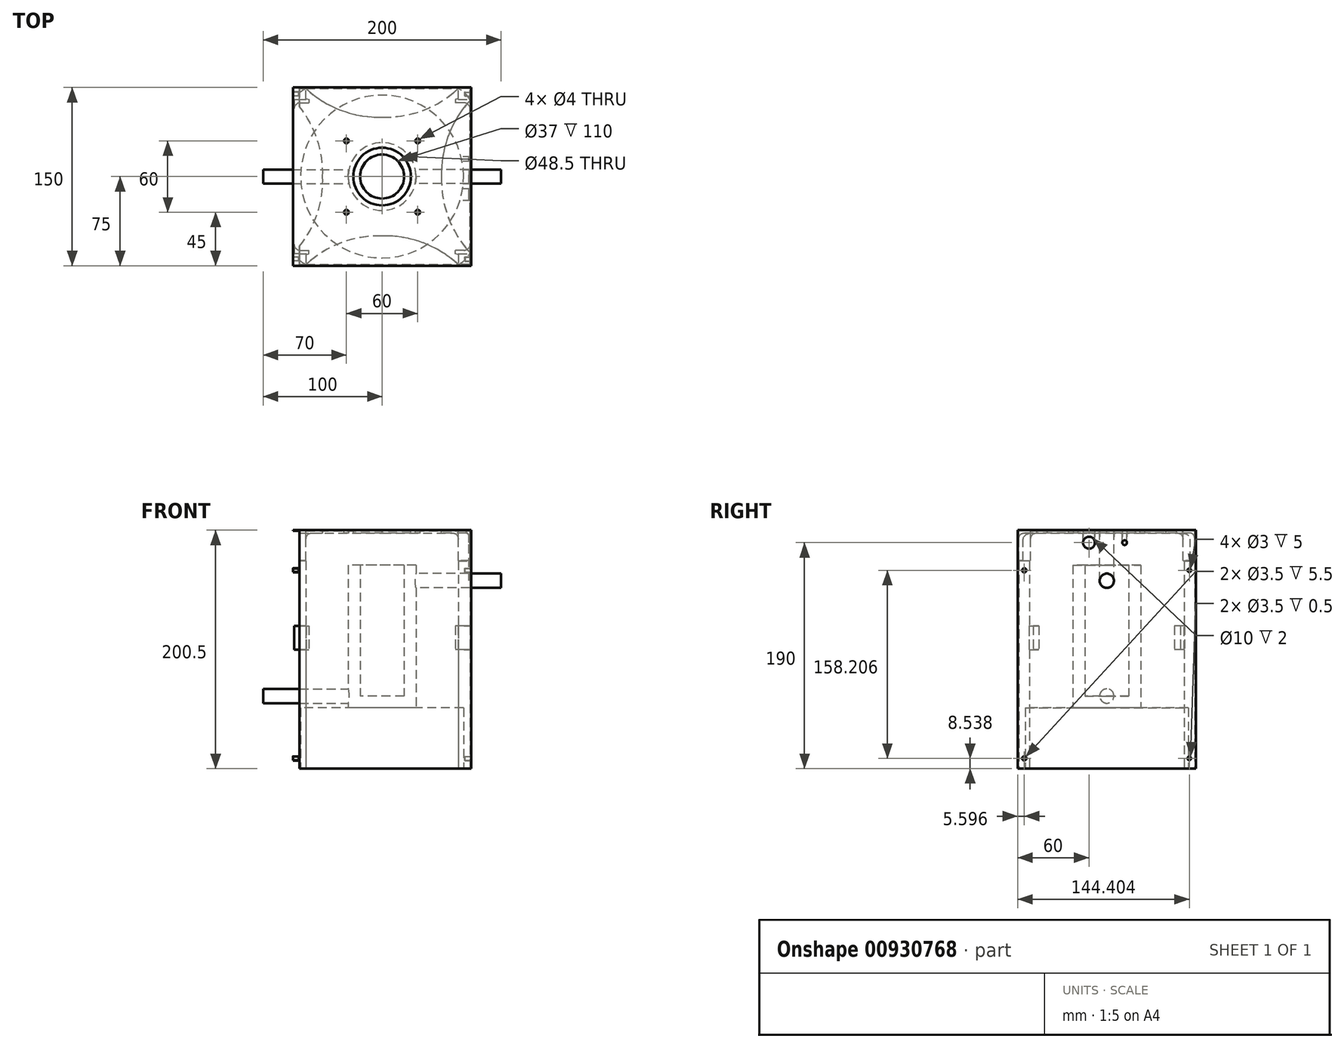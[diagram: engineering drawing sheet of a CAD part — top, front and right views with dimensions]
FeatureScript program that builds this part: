
annotation { "Feature Type Name" : "Feature", "Feature Type Description" : "" }
export const myFeature = defineFeature(function(context is Context, id is Id, definition is map)
    precondition{}
    {
        {
            var Q0;
            Q0=qCreatedBy(makeId("Top.planeOp"),FACE);
            var sketch = newSketch(context, id + "F0", { "sketchPlane" : qUnion([Q0])});
            skCircle(sketch, "E0", {"center": v(0, 0) * mm, "radius": 68.5 * mm});
            skSolve(sketch);
        }
        {
            var Q0;
            Q0 = qSketchRegion(id + "F0", true);
            extrude(context, id + "F1", {"entities" : qUnion([Q0]), "depth" : 51 * mm, "offsetDistance" : 25 * mm});
        }
        {
            var Q0;
            Q0=makeQuery(id+"F1.opExtrude","CAP_FACE",FACE,{"disambiguationData":[OSD([sQuery(id+"F0.wireOp",EDGE,"E0")])],"isStart":false});
            var sketch = newSketch(context, id + "F2", { "sketchPlane" : qUnion([Q0])});
            skCircle(sketch, "E1", {"center": v(0, 0) * mm, "radius": 28.5 * mm});
            skSolve(sketch);
        }
        {
            var Q0;
            Q0 = qSketchRegion(id + "F2", true);
            extrude(context, id + "F3", {"entities" : qUnion([Q0]), "depth" : 120 * mm, "offsetDistance" : 25 * mm});
        }
        {
            var Q0;
            Q0=qCreatedBy(makeId("Right.planeOp"),FACE);
            var sketch = newSketch(context, id + "F4", { "sketchPlane" : qUnion([Q0])});
            skCircle(sketch, "E2", {"center": v(0, 158) * mm, "radius": 6 * mm});
            skCircle(sketch, "E3", {"center": v(0, 61) * mm, "radius": 6 * mm});
            skSolve(sketch);
        }
        {
            var Q0;
            Q0=makeQuery(id+"F4.imprint","IMPRINT",FACE,{"disambiguationData":[TD([[makeQuery(id+"F4.imprint","IMPRINT",EDGE,{"derivedFrom":sQuery(id+"F4.wireOp",EDGE,"E2")}),1.0]])]});
            extrude(context, id + "F5", {"entities" : qUnion([Q0]), "operationType" : NewBodyOperationType.ADD, "depth" : 100 * mm, "offsetDistance" : 25 * mm});
        }
        {
            var Q0;
            Q0=makeQuery(id+"F4.imprint","IMPRINT",FACE,{"disambiguationData":[TD([[makeQuery(id+"F4.imprint","IMPRINT",EDGE,{"derivedFrom":sQuery(id+"F4.wireOp",EDGE,"E3")}),1.0]])]});
            extrude(context, id + "F6", {"entities" : qUnion([Q0]), "operationType" : NewBodyOperationType.ADD, "oppositeDirection" : true, "depth" : 100 * mm, "offsetDistance" : 25 * mm});
        }
        {
            var Q0;
            Q0=makeQuery(id+"F3.opExtrude","CAP_FACE",FACE,{"disambiguationData":[OSD([sQuery(id+"F2.wireOp",EDGE,"E1")])],"isStart":false});
            shell(context, id + "F7", {"entities" : qUnion([Q0]), "thickness" : 10 * mm});
        }
        {
            var Q0;
            Q0=qCreatedBy(makeId("Front.planeOp"),FACE);
            var sketch = newSketch(context, id + "F8", { "sketchPlane" : qUnion([Q0])});
            skLineSegment(sketch, "E4.bottom", {"start": v(-75, 0) * mm, "end": v(75, 0) * mm});
            skLineSegment(sketch, "E4.top", {"start": v(-75, 180) * mm, "end": v(75, 180) * mm});
            skLineSegment(sketch, "E4.left", {"start": v(-75, 0) * mm, "end": v(-75, 180) * mm});
            skLineSegment(sketch, "E4.right", {"start": v(75, 0) * mm, "end": v(75, 180) * mm});
            skSolve(sketch);
        }
        {
            var Q0;
            Q0=qCreatedBy(makeId("Top.planeOp"),FACE);
            cPlane(context, id + "F9", {"entities" : qUnion([Q0]), "cplaneType" : CPlaneType.OFFSET, "offset" : 200 * mm, "width" : 150 * mm, "height" : 150 * mm});
        }
        {
            var Q0;
            Q0=qCreatedBy(id+"F9.planeOp",FACE);
            var sketch = newSketch(context, id + "F10", { "sketchPlane" : qUnion([Q0])});
            skCircle(sketch, "E5", {"center": v(0, 0) * mm, "radius": 24.25 * mm});
            skCircle(sketch, "E6", {"center": v(-30, 30) * mm, "radius": 2 * mm});
            skCircle(sketch, "E7.1.0", {"center": v(-30, -30) * mm, "radius": 2 * mm});
            skCircle(sketch, "E7.2.0", {"center": v(30, -30) * mm, "radius": 2 * mm});
            skCircle(sketch, "E7.3.0", {"center": v(30, 30) * mm, "radius": 2 * mm});
            skLineSegment(sketch, "E8.bottom", {"start": v(75, 75) * mm, "end": v(-75, 75) * mm});
            skLineSegment(sketch, "E8.top", {"start": v(75, -75) * mm, "end": v(-75, -75) * mm});
            skLineSegment(sketch, "E8.left", {"start": v(75, 75) * mm, "end": v(75, -75) * mm});
            skLineSegment(sketch, "E8.right", {"start": v(-75, 75) * mm, "end": v(-75, -75) * mm});
            skLineSegment(sketch, "E9.bottom", {"start": v(-74, 74) * mm, "end": v(-64, 74) * mm});
            skLineSegment(sketch, "E9.top", {"start": v(-74, 64) * mm, "end": v(-64, 64) * mm});
            skLineSegment(sketch, "E9.left", {"start": v(-74, 74) * mm, "end": v(-74, 64) * mm});
            skLineSegment(sketch, "E9.right", {"start": v(-64, 74) * mm, "end": v(-64, 64) * mm});
            skArc(sketch, "E10", {"start": v(-64, 74) * mm, "mid": v(-69.91, 69.91) * mm, "end": v(-74, 64) * mm});
            skLineSegment(sketch, "E11.1.0", {"start": v(-74, -74) * mm, "end": v(-74, -64) * mm});
            skLineSegment(sketch, "E11.1.1", {"start": v(-74, -74) * mm, "end": v(-64, -74) * mm});
            skArc(sketch, "E11.1.2", {"start": v(-74, -64) * mm, "mid": v(-69.91, -69.91) * mm, "end": v(-64, -74) * mm});
            skLineSegment(sketch, "E11.2.0", {"start": v(74, -74) * mm, "end": v(64, -74) * mm});
            skLineSegment(sketch, "E11.2.1", {"start": v(74, -74) * mm, "end": v(74, -64) * mm});
            skArc(sketch, "E11.2.2", {"start": v(64, -74) * mm, "mid": v(69.91, -69.91) * mm, "end": v(74, -64) * mm});
            skLineSegment(sketch, "E11.3.0", {"start": v(74, 74) * mm, "end": v(74, 64) * mm});
            skLineSegment(sketch, "E11.3.1", {"start": v(74, 74) * mm, "end": v(64, 74) * mm});
            skArc(sketch, "E11.3.2", {"start": v(74, 64) * mm, "mid": v(69.91, 69.91) * mm, "end": v(64, 74) * mm});
            skCircle(sketch, "E12", {"center": v(0, 0) * mm, "radius": 50 * mm});
            skArc(sketch, "E13", {"start": v(-50, 0) * mm, "mid": v(-55.69, 34.37) * mm, "end": v(-74, 64) * mm});
            skArc(sketch, "E14", {"start": v(-64, 74) * mm, "mid": v(-34.37, 55.69) * mm, "end": v(0, 50) * mm});
            skArc(sketch, "E15.1.0", {"start": v(-74, -64) * mm, "mid": v(-55.69, -34.37) * mm, "end": v(-50, 0) * mm});
            skArc(sketch, "E15.1.1", {"start": v(0, -50) * mm, "mid": v(-34.37, -55.69) * mm, "end": v(-64, -74) * mm});
            skArc(sketch, "E15.2.0", {"start": v(64, -74) * mm, "mid": v(34.37, -55.69) * mm, "end": v(0, -50) * mm});
            skArc(sketch, "E15.2.1", {"start": v(50, 0) * mm, "mid": v(55.69, -34.37) * mm, "end": v(74, -64) * mm});
            skArc(sketch, "E15.3.0", {"start": v(74, 64) * mm, "mid": v(55.69, 34.37) * mm, "end": v(50, 0) * mm});
            skArc(sketch, "E15.3.1", {"start": v(0, 50) * mm, "mid": v(34.37, 55.69) * mm, "end": v(64, 74) * mm});
            skSolve(sketch);
        }
        {
            var Q0;
            Q0=qCreatedBy(id+"F9.planeOp",FACE);
            var sketch = newSketch(context, id + "F11", { "sketchPlane" : qUnion([Q0])});
            skLineSegment(sketch, "E16.bottom", {"start": v(75, 75) * mm, "end": v(-75, 75) * mm});
            skLineSegment(sketch, "E16.top", {"start": v(75, -75) * mm, "end": v(-75, -75) * mm});
            skLineSegment(sketch, "E16.left", {"start": v(75, 75) * mm, "end": v(75, -75) * mm});
            skLineSegment(sketch, "E16.right", {"start": v(-75, 75) * mm, "end": v(-75, -75) * mm});
            skPoint(sketch, "E16.middle", {"position": v(0, 0) * mm});
            skSolve(sketch);
        }
        {
            var Q0;
            Q0=makeQuery(id+"F10.imprint","IMPRINT",FACE,{"disambiguationData":[TD([[makeQuery(id+"F10.imprint","IMPRINT",EDGE,{"derivedFrom":sQuery(id+"F10.wireOp",EDGE,"E9.bottom")}),-1.0]])]});
            var Q1;
            Q1=makeQuery(id+"F10.imprint","IMPRINT",FACE,{"disambiguationData":[TD([[makeQuery(id+"F10.imprint","IMPRINT",EDGE,{"derivedFrom":sQuery(id+"F10.wireOp",EDGE,"E9.top")}),1.0]])]});
            var Q2;
            {var subQ2=sQuery(id+"F10.wireOp",EDGE,"E9.top");Q2=makeQuery(id+"F10.imprint","IMPRINT",FACE,{"disambiguationData":[TD([[makeQuery(id+"F10.imprint","IMPRINT",EDGE,{"derivedFrom":subQ2}),-1.0]])]});}
            var Q3;
            Q3=makeQuery(id+"F10.imprint","IMPRINT",FACE,{"disambiguationData":[TD([[makeQuery(id+"F10.imprint","IMPRINT",EDGE,{"derivedFrom":sQuery(id+"F10.wireOp",EDGE,"E5")}),-1.0]])]});
            var Q4;
            {var subQ0=sQuery(id+"F10.wireOp",EDGE,"E11.3.2");Q4=makeQuery(id+"F10.imprint","IMPRINT",FACE,{"disambiguationData":[TD([[makeQuery(id+"F10.imprint","IMPRINT",EDGE,{"derivedFrom":subQ0}),1.0]])]});}
            var Q5;
            Q5=makeQuery(id+"F10.imprint","IMPRINT",FACE,{"disambiguationData":[TD([[makeQuery(id+"F10.imprint","IMPRINT",EDGE,{"derivedFrom":sQuery(id+"F10.wireOp",EDGE,"E11.3.0")}),-1.0]])]});
            var Q6;
            Q6=makeQuery(id+"F10.imprint","IMPRINT",FACE,{"disambiguationData":[TD([[makeQuery(id+"F10.imprint","IMPRINT",EDGE,{"derivedFrom":sQuery(id+"F10.wireOp",EDGE,"E11.2.0")}),-1.0]])]});
            var Q7;
            {var subQ0=sQuery(id+"F10.wireOp",EDGE,"E11.2.2");Q7=makeQuery(id+"F10.imprint","IMPRINT",FACE,{"disambiguationData":[TD([[makeQuery(id+"F10.imprint","IMPRINT",EDGE,{"derivedFrom":subQ0}),1.0]])]});}
            var Q8;
            {var subQ0=sQuery(id+"F10.wireOp",EDGE,"E11.1.2");Q8=makeQuery(id+"F10.imprint","IMPRINT",FACE,{"disambiguationData":[TD([[makeQuery(id+"F10.imprint","IMPRINT",EDGE,{"derivedFrom":subQ0}),1.0]])]});}
            var Q9;
            Q9=makeQuery(id+"F10.imprint","IMPRINT",FACE,{"disambiguationData":[TD([[makeQuery(id+"F10.imprint","IMPRINT",EDGE,{"derivedFrom":sQuery(id+"F10.wireOp",EDGE,"E11.1.0")}),-1.0]])]});
            extrude(context, id + "F12", {"entities" : qUnion([Q0, Q1, Q2, Q3, Q4, Q5, Q6, Q7, Q8, Q9]), "oppositeDirection" : true, "depth" : 2 * mm, "offsetDistance" : 25 * mm});
        }
        {
            var Q0;
            Q0 = qSketchRegion(id + "F11", true);
            extrude(context, id + "F13", {"entities" : qUnion([Q0]), "operationType" : NewBodyOperationType.ADD, "depth" : 0.5 * mm, "offsetDistance" : 25 * mm});
        }
        {
            var Q0;
            Q0=makeQuery(id+"F10.imprint","IMPRINT",FACE,{"disambiguationData":[TD([[makeQuery(id+"F10.imprint","IMPRINT",EDGE,{"derivedFrom":sQuery(id+"F10.wireOp",EDGE,"E9.bottom")}),-1.0]])]});
            var Q1;
            Q1=makeQuery(id+"F10.imprint","IMPRINT",FACE,{"disambiguationData":[TD([[makeQuery(id+"F10.imprint","IMPRINT",EDGE,{"derivedFrom":sQuery(id+"F10.wireOp",EDGE,"E11.1.0")}),-1.0]])]});
            var Q2;
            Q2=makeQuery(id+"F10.imprint","IMPRINT",FACE,{"disambiguationData":[TD([[makeQuery(id+"F10.imprint","IMPRINT",EDGE,{"derivedFrom":sQuery(id+"F10.wireOp",EDGE,"E11.2.0")}),-1.0]])]});
            var Q3;
            Q3=makeQuery(id+"F10.imprint","IMPRINT",FACE,{"disambiguationData":[TD([[makeQuery(id+"F10.imprint","IMPRINT",EDGE,{"derivedFrom":sQuery(id+"F10.wireOp",EDGE,"E11.3.0")}),-1.0]])]});
            extrude(context, id + "F14", {"entities" : qUnion([Q0, Q1, Q2, Q3]), "operationType" : NewBodyOperationType.ADD, "oppositeDirection" : true, "depth" : 25 * mm, "offsetDistance" : 25 * mm});
        }
        {
            var Q0;
            Q0=makeQuery(id+"F10.imprint","IMPRINT",FACE,{"disambiguationData":[TD([[makeQuery(id+"F10.imprint","IMPRINT",EDGE,{"derivedFrom":sQuery(id+"F10.wireOp",EDGE,"E6")}),1.0]])]});
            var Q1;
            Q1=makeQuery(id+"F10.imprint","IMPRINT",FACE,{"disambiguationData":[TD([[makeQuery(id+"F10.imprint","IMPRINT",EDGE,{"derivedFrom":sQuery(id+"F10.wireOp",EDGE,"E7.3.0")}),1.0]])]});
            var Q2;
            Q2=makeQuery(id+"F10.imprint","IMPRINT",FACE,{"disambiguationData":[TD([[makeQuery(id+"F10.imprint","IMPRINT",EDGE,{"derivedFrom":sQuery(id+"F10.wireOp",EDGE,"E7.2.0")}),1.0]])]});
            var Q3;
            Q3=makeQuery(id+"F10.imprint","IMPRINT",FACE,{"disambiguationData":[TD([[makeQuery(id+"F10.imprint","IMPRINT",EDGE,{"derivedFrom":sQuery(id+"F10.wireOp",EDGE,"E7.1.0")}),1.0]])]});
            var Q4;
            Q4=makeQuery(id+"F10.imprint","IMPRINT",FACE,{"disambiguationData":[TD([[makeQuery(id+"F10.imprint","IMPRINT",EDGE,{"derivedFrom":sQuery(id+"F10.wireOp",EDGE,"E5")}),1.0]])]});
            extrude(context, id + "F15", {"entities" : qUnion([Q0, Q1, Q2, Q3, Q4]), "operationType" : NewBodyOperationType.REMOVE, "endBound" : BoundingType.SYMMETRIC, "oppositeDirection" : true, "depth" : 25 * mm, "offsetDistance" : 25 * mm});
        }
        {
            var Q0;
            Q0=makeQuery(id+"F14.boolean.opBoolean","INTERSECT",EDGE,{"derivedFrom":[makeQuery(id+"F12.opExtrude","CAP_FACE",FACE,{"disambiguationData":[OSD([sQuery(id+"F10.wireOp",EDGE,"E5"),sQuery(id+"F10.wireOp",EDGE,"E6"),sQuery(id+"F10.wireOp",EDGE,"E7.1.0"),sQuery(id+"F10.wireOp",EDGE,"E7.2.0"),sQuery(id+"F10.wireOp",EDGE,"E7.3.0"),sQuery(id+"F10.wireOp",EDGE,"E9.bottom"),sQuery(id+"F10.wireOp",EDGE,"E9.left"),sQuery(id+"F10.wireOp",EDGE,"E11.1.0"),sQuery(id+"F10.wireOp",EDGE,"E11.1.1"),sQuery(id+"F10.wireOp",EDGE,"E11.2.0"),sQuery(id+"F10.wireOp",EDGE,"E11.2.1"),sQuery(id+"F10.wireOp",EDGE,"E11.3.0"),sQuery(id+"F10.wireOp",EDGE,"E11.3.1"),sQuery(id+"F10.wireOp",EDGE,"E13"),sQuery(id+"F10.wireOp",EDGE,"E14"),sQuery(id+"F10.wireOp",EDGE,"E15.1.0"),sQuery(id+"F10.wireOp",EDGE,"E15.1.1"),sQuery(id+"F10.wireOp",EDGE,"E15.2.0"),sQuery(id+"F10.wireOp",EDGE,"E15.2.1"),sQuery(id+"F10.wireOp",EDGE,"E15.3.0"),sQuery(id+"F10.wireOp",EDGE,"E15.3.1")])],"isStart":false}),makeQuery(id+"F14.opExtrude","SWEPT_FACE",FACE,{"disambiguationData":[OSD([sQuery(id+"F10.wireOp",EDGE,"E11.1.2")])]})]});
            var Q1;
            Q1=makeQuery(id+"F14.boolean.opBoolean","INTERSECT",EDGE,{"derivedFrom":[makeQuery(id+"F12.opExtrude","CAP_FACE",FACE,{"disambiguationData":[OSD([sQuery(id+"F10.wireOp",EDGE,"E5"),sQuery(id+"F10.wireOp",EDGE,"E6"),sQuery(id+"F10.wireOp",EDGE,"E7.1.0"),sQuery(id+"F10.wireOp",EDGE,"E7.2.0"),sQuery(id+"F10.wireOp",EDGE,"E7.3.0"),sQuery(id+"F10.wireOp",EDGE,"E9.bottom"),sQuery(id+"F10.wireOp",EDGE,"E9.left"),sQuery(id+"F10.wireOp",EDGE,"E11.1.0"),sQuery(id+"F10.wireOp",EDGE,"E11.1.1"),sQuery(id+"F10.wireOp",EDGE,"E11.2.0"),sQuery(id+"F10.wireOp",EDGE,"E11.2.1"),sQuery(id+"F10.wireOp",EDGE,"E11.3.0"),sQuery(id+"F10.wireOp",EDGE,"E11.3.1"),sQuery(id+"F10.wireOp",EDGE,"E13"),sQuery(id+"F10.wireOp",EDGE,"E14"),sQuery(id+"F10.wireOp",EDGE,"E15.1.0"),sQuery(id+"F10.wireOp",EDGE,"E15.1.1"),sQuery(id+"F10.wireOp",EDGE,"E15.2.0"),sQuery(id+"F10.wireOp",EDGE,"E15.2.1"),sQuery(id+"F10.wireOp",EDGE,"E15.3.0"),sQuery(id+"F10.wireOp",EDGE,"E15.3.1")])],"isStart":false}),makeQuery(id+"F14.opExtrude","SWEPT_FACE",FACE,{"disambiguationData":[OSD([sQuery(id+"F10.wireOp",EDGE,"E11.3.2")])]})]});
            var Q2;
            Q2=makeQuery(id+"F14.boolean.opBoolean","INTERSECT",EDGE,{"derivedFrom":[makeQuery(id+"F12.opExtrude","CAP_FACE",FACE,{"disambiguationData":[OSD([sQuery(id+"F10.wireOp",EDGE,"E5"),sQuery(id+"F10.wireOp",EDGE,"E6"),sQuery(id+"F10.wireOp",EDGE,"E7.1.0"),sQuery(id+"F10.wireOp",EDGE,"E7.2.0"),sQuery(id+"F10.wireOp",EDGE,"E7.3.0"),sQuery(id+"F10.wireOp",EDGE,"E9.bottom"),sQuery(id+"F10.wireOp",EDGE,"E9.left"),sQuery(id+"F10.wireOp",EDGE,"E11.1.0"),sQuery(id+"F10.wireOp",EDGE,"E11.1.1"),sQuery(id+"F10.wireOp",EDGE,"E11.2.0"),sQuery(id+"F10.wireOp",EDGE,"E11.2.1"),sQuery(id+"F10.wireOp",EDGE,"E11.3.0"),sQuery(id+"F10.wireOp",EDGE,"E11.3.1"),sQuery(id+"F10.wireOp",EDGE,"E13"),sQuery(id+"F10.wireOp",EDGE,"E14"),sQuery(id+"F10.wireOp",EDGE,"E15.1.0"),sQuery(id+"F10.wireOp",EDGE,"E15.1.1"),sQuery(id+"F10.wireOp",EDGE,"E15.2.0"),sQuery(id+"F10.wireOp",EDGE,"E15.2.1"),sQuery(id+"F10.wireOp",EDGE,"E15.3.0"),sQuery(id+"F10.wireOp",EDGE,"E15.3.1")])],"isStart":false}),makeQuery(id+"F14.opExtrude","SWEPT_FACE",FACE,{"disambiguationData":[OSD([sQuery(id+"F10.wireOp",EDGE,"E10")])]})]});
            var Q3;
            Q3=makeQuery(id+"F14.boolean.opBoolean","INTERSECT",EDGE,{"derivedFrom":[makeQuery(id+"F12.opExtrude","CAP_FACE",FACE,{"disambiguationData":[OSD([sQuery(id+"F10.wireOp",EDGE,"E5"),sQuery(id+"F10.wireOp",EDGE,"E6"),sQuery(id+"F10.wireOp",EDGE,"E7.1.0"),sQuery(id+"F10.wireOp",EDGE,"E7.2.0"),sQuery(id+"F10.wireOp",EDGE,"E7.3.0"),sQuery(id+"F10.wireOp",EDGE,"E9.bottom"),sQuery(id+"F10.wireOp",EDGE,"E9.left"),sQuery(id+"F10.wireOp",EDGE,"E11.1.0"),sQuery(id+"F10.wireOp",EDGE,"E11.1.1"),sQuery(id+"F10.wireOp",EDGE,"E11.2.0"),sQuery(id+"F10.wireOp",EDGE,"E11.2.1"),sQuery(id+"F10.wireOp",EDGE,"E11.3.0"),sQuery(id+"F10.wireOp",EDGE,"E11.3.1"),sQuery(id+"F10.wireOp",EDGE,"E13"),sQuery(id+"F10.wireOp",EDGE,"E14"),sQuery(id+"F10.wireOp",EDGE,"E15.1.0"),sQuery(id+"F10.wireOp",EDGE,"E15.1.1"),sQuery(id+"F10.wireOp",EDGE,"E15.2.0"),sQuery(id+"F10.wireOp",EDGE,"E15.2.1"),sQuery(id+"F10.wireOp",EDGE,"E15.3.0"),sQuery(id+"F10.wireOp",EDGE,"E15.3.1")])],"isStart":false}),makeQuery(id+"F14.opExtrude","SWEPT_FACE",FACE,{"disambiguationData":[OSD([sQuery(id+"F10.wireOp",EDGE,"E11.2.2")])]})]});
            fillet(context, id + "F16", {"entities" : qUnion([Q0, Q1, Q2, Q3]), "tangentPropagation" : true, "radius" : 5 * mm, "defaultsChanged" : false, "vertexSettings" : [], "allowEdgeOverflow" : false});
        }
        {
            var Q0;
            Q0=makeQuery(id+"F8.imprint","IMPRINT",FACE,{"disambiguationData":[TD([[makeQuery(id+"F8.imprint","IMPRINT",EDGE,{"derivedFrom":sQuery(id+"F8.wireOp",EDGE,"E4.bottom")}),1.0]])]});
            cPlane(context, id + "F17", {"entities" : qUnion([Q0]), "cplaneType" : CPlaneType.OFFSET, "offset" : 75 * mm, "width" : 150 * mm, "height" : 150 * mm});
        }
        {
            var Q0;
            Q0=qCreatedBy(id+"F17.planeOp",FACE);
            var sketch = newSketch(context, id + "F18", { "sketchPlane" : qUnion([Q0])});
            skLineSegment(sketch, "E17.bottom", {"start": v(-75, 0) * mm, "end": v(75, 0) * mm});
            skLineSegment(sketch, "E17.top", {"start": v(-75, 200) * mm, "end": v(75, 200) * mm});
            skLineSegment(sketch, "E17.left", {"start": v(-75, 0) * mm, "end": v(-75, 200) * mm});
            skLineSegment(sketch, "E17.right", {"start": v(75, 0) * mm, "end": v(75, 200) * mm});
            skLineSegment(sketch, "E18", {"start": v(-74, 200) * mm, "end": v(-74, 0) * mm});
            skLineSegment(sketch, "E19", {"start": v(-64, 200) * mm, "end": v(-64, 0) * mm});
            skLineSegment(sketch, "E20", {"start": v(74, 200) * mm, "end": v(74, 0) * mm});
            skLineSegment(sketch, "E21", {"start": v(64, 200) * mm, "end": v(64, 0) * mm});
            skLineSegment(sketch, "E22", {"start": v(-64, 174.5) * mm, "end": v(-74, 174.5) * mm});
            skLineSegment(sketch, "E23", {"start": v(64, 174.5) * mm, "end": v(74, 174.5) * mm});
            skSolve(sketch);
        }
        {
            var Q0;
            {var subQ0=sQuery(id+"F18.wireOp",EDGE,"E19");Q0=makeQuery(id+"F18.imprint","IMPRINT",FACE,{"disambiguationData":[TD([[makeQuery(id+"F18.imprint","IMPRINT",EDGE,{"derivedFrom":subQ0}),1.0]])]});}
            var Q1;
            {var subQ0=sQuery(id+"F18.wireOp",EDGE,"E20");Q1=makeQuery(id+"F18.imprint","IMPRINT",FACE,{"disambiguationData":[TD([[makeQuery(id+"F18.imprint","IMPRINT",EDGE,{"derivedFrom":subQ0}),-1.0]])]});}
            var Q2;
            {var subQ5=sQuery(id+"F18.wireOp",EDGE,"E22");Q2=makeQuery(id+"F18.imprint","IMPRINT",FACE,{"disambiguationData":[TD([[makeQuery(id+"F18.imprint","IMPRINT",EDGE,{"derivedFrom":subQ5}),-1.0]])]});}
            var Q3;
            {var subQ5=sQuery(id+"F18.wireOp",EDGE,"E22");Q3=makeQuery(id+"F18.imprint","IMPRINT",FACE,{"disambiguationData":[TD([[makeQuery(id+"F18.imprint","IMPRINT",EDGE,{"derivedFrom":subQ5}),1.0]])]});}
            extrude(context, id + "F19", {"entities" : qUnion([Q0, Q1, Q2, Q3]), "oppositeDirection" : true, "depth" : 1 * mm, "offsetDistance" : 25 * mm});
        }
        {
            var Q0;
            {var subQ5=sQuery(id+"F18.wireOp",EDGE,"E22");Q0=makeQuery(id+"F18.imprint","IMPRINT",FACE,{"disambiguationData":[TD([[makeQuery(id+"F18.imprint","IMPRINT",EDGE,{"derivedFrom":subQ5}),1.0]])]});}
            var Q1;
            {var subQ5=sQuery(id+"F18.wireOp",EDGE,"E23");Q1=makeQuery(id+"F18.imprint","IMPRINT",FACE,{"disambiguationData":[TD([[makeQuery(id+"F18.imprint","IMPRINT",EDGE,{"derivedFrom":subQ5}),-1.0]])]});}
            extrude(context, id + "F20", {"entities" : qUnion([Q0, Q1]), "operationType" : NewBodyOperationType.ADD, "oppositeDirection" : true, "depth" : 10 * mm, "offsetDistance" : 25 * mm});
        }
        {
            var Q0;
            Q0=qCreatedBy(makeId("Right.planeOp"),FACE);
            cPlane(context, id + "F21", {"entities" : qUnion([Q0]), "cplaneType" : CPlaneType.OFFSET, "offset" : 75 * mm, "width" : 150 * mm, "height" : 150 * mm});
        }
        {
            var Q0;
            Q0=qCreatedBy(id+"F21.planeOp",FACE);
            var sketch = newSketch(context, id + "F22", { "sketchPlane" : qUnion([Q0])});
            skLineSegment(sketch, "E24.bottom", {"start": v(-75, 0) * mm, "end": v(75, 0) * mm});
            skLineSegment(sketch, "E24.top", {"start": v(-75, 200) * mm, "end": v(75, 200) * mm});
            skLineSegment(sketch, "E24.left", {"start": v(-75, 0) * mm, "end": v(-75, 200) * mm});
            skLineSegment(sketch, "E24.right", {"start": v(75, 0) * mm, "end": v(75, 200) * mm});
            skCircle(sketch, "E25.0", {"center": v(0, 158) * mm, "radius": 6 * mm});
            skCircle(sketch, "E26", {"center": v(-15, 190) * mm, "radius": 5 * mm});
            skCircle(sketch, "E27", {"center": v(15, 190) * mm, "radius": 2 * mm});
            skLineSegment(sketch, "E28", {"start": v(15, 190) * mm, "end": v(-15, 190) * mm, "construction": true});
            skLineSegment(sketch, "E29", {"start": v(0, 0) * mm, "end": v(0, 190) * mm, "construction": true});
            skLineSegment(sketch, "E30", {"start": v(6, 158) * mm, "end": v(6, 200) * mm});
            skLineSegment(sketch, "E31", {"start": v(-6, 158) * mm, "end": v(-6, 200) * mm});
            skLineSegment(sketch, "E32", {"start": v(-10, 190) * mm, "end": v(-10, 200) * mm});
            skLineSegment(sketch, "E33", {"start": v(-20, 190) * mm, "end": v(-20, 200) * mm});
            skLineSegment(sketch, "E34", {"start": v(13, 190) * mm, "end": v(13, 200) * mm});
            skLineSegment(sketch, "E35", {"start": v(17, 190) * mm, "end": v(17, 200) * mm});
            skCircle(sketch, "E36", {"center": v(-69.4, 166.74) * mm, "radius": 1.5 * mm});
            skCircle(sketch, "E37", {"center": v(-69.4, 166.74) * mm, "radius": 1.75 * mm});
            skCircle(sketch, "E38", {"center": v(-69.4, 8.54) * mm, "radius": 1.5 * mm});
            skCircle(sketch, "E39", {"center": v(-69.4, 8.54) * mm, "radius": 1.75 * mm});
            skCircle(sketch, "E40.MirrorC", {"center": v(69.4, 166.74) * mm, "radius": 1.5 * mm});
            skCircle(sketch, "E41.MirrorC", {"center": v(69.4, 166.74) * mm, "radius": 1.75 * mm});
            skCircle(sketch, "E42.MirrorC", {"center": v(69.4, 8.54) * mm, "radius": 1.5 * mm});
            skCircle(sketch, "E43.MirrorC", {"center": v(69.4, 8.54) * mm, "radius": 1.75 * mm});
            skSolve(sketch);
        }
        {
            var Q0;
            Q0=makeQuery(id+"F22.imprint","IMPRINT",FACE,{"disambiguationData":[TD([[makeQuery(id+"F22.imprint","IMPRINT",EDGE,{"derivedFrom":sQuery(id+"F22.wireOp",EDGE,"E24.bottom")}),1.0]])]});
            var Q1;
            Q1=makeQuery(id+"F22.imprint","IMPRINT",FACE,{"disambiguationData":[TD([[makeQuery(id+"F22.imprint","IMPRINT",EDGE,{"derivedFrom":sQuery(id+"F22.wireOp",EDGE,"E36")}),-1.0]])]});
            var Q2;
            Q2=makeQuery(id+"F22.imprint","IMPRINT",FACE,{"disambiguationData":[TD([[makeQuery(id+"F22.imprint","IMPRINT",EDGE,{"derivedFrom":sQuery(id+"F22.wireOp",EDGE,"E36")}),1.0]])]});
            var Q3;
            Q3=makeQuery(id+"F22.imprint","IMPRINT",FACE,{"disambiguationData":[TD([[makeQuery(id+"F22.imprint","IMPRINT",EDGE,{"derivedFrom":sQuery(id+"F22.wireOp",EDGE,"E40.MirrorC")}),1.0]])]});
            var Q4;
            Q4=makeQuery(id+"F22.imprint","IMPRINT",FACE,{"disambiguationData":[TD([[makeQuery(id+"F22.imprint","IMPRINT",EDGE,{"derivedFrom":sQuery(id+"F22.wireOp",EDGE,"E40.MirrorC")}),-1.0]])]});
            var Q5;
            Q5=makeQuery(id+"F22.imprint","IMPRINT",FACE,{"disambiguationData":[TD([[makeQuery(id+"F22.imprint","IMPRINT",EDGE,{"derivedFrom":sQuery(id+"F22.wireOp",EDGE,"E38")}),1.0]])]});
            var Q6;
            Q6=makeQuery(id+"F22.imprint","IMPRINT",FACE,{"disambiguationData":[TD([[makeQuery(id+"F22.imprint","IMPRINT",EDGE,{"derivedFrom":sQuery(id+"F22.wireOp",EDGE,"E38")}),-1.0]])]});
            var Q7;
            Q7=makeQuery(id+"F22.imprint","IMPRINT",FACE,{"disambiguationData":[TD([[makeQuery(id+"F22.imprint","IMPRINT",EDGE,{"derivedFrom":sQuery(id+"F22.wireOp",EDGE,"E42.MirrorC")}),-1.0]])]});
            var Q8;
            Q8=makeQuery(id+"F22.imprint","IMPRINT",FACE,{"disambiguationData":[TD([[makeQuery(id+"F22.imprint","IMPRINT",EDGE,{"derivedFrom":sQuery(id+"F22.wireOp",EDGE,"E42.MirrorC")}),1.0]])]});
            extrude(context, id + "F23", {"entities" : qUnion([Q0, Q1, Q2, Q3, Q4, Q5, Q6, Q7, Q8]), "oppositeDirection" : true, "depth" : 1 * mm, "offsetDistance" : 25 * mm});
        }
        {
            var Q0;
            {var subQ0=sQuery(id+"F22.wireOp",EDGE,"E32");Q0=makeQuery(id+"F22.imprint","IMPRINT",FACE,{"disambiguationData":[TD([[makeQuery(id+"F22.imprint","IMPRINT",EDGE,{"derivedFrom":subQ0}),1.0]])]});}
            var Q1;
            {var subQ0=sQuery(id+"F22.wireOp",EDGE,"E30");Q1=makeQuery(id+"F22.imprint","IMPRINT",FACE,{"disambiguationData":[TD([[makeQuery(id+"F22.imprint","IMPRINT",EDGE,{"derivedFrom":subQ0}),1.0]])]});}
            var Q2;
            {var subQ0=sQuery(id+"F22.wireOp",EDGE,"E34");Q2=makeQuery(id+"F22.imprint","IMPRINT",FACE,{"disambiguationData":[TD([[makeQuery(id+"F22.imprint","IMPRINT",EDGE,{"derivedFrom":subQ0}),-1.0]])]});}
            extrude(context, id + "F24", {"entities" : qUnion([Q0, Q1, Q2]), "operationType" : NewBodyOperationType.ADD, "oppositeDirection" : true, "depth" : 2 * mm, "offsetDistance" : 25 * mm});
        }
        {
            var Q0;
            {var subQ0=sQuery(id+"F22.wireOp",EDGE,"E24.top");Q0=makeQuery(id+"F24.opExtrude","CAP_EDGE",EDGE,{"disambiguationData":[OSD([subQ0]),TDD([makeQuery(id+"F22.imprint","IMPRINT",EDGE,{"disambiguationData":[TD([[makeQuery(id+"F22.imprint","INTERSECT",VERTEX,{"derivedFrom":[subQ0,sQuery(id+"F22.wireOp",EDGE,"E34")]}),-1.0]])],"derivedFrom":subQ0})])],"isStart":false});}
            var Q1;
            {var subQ0=sQuery(id+"F22.wireOp",EDGE,"E24.top");Q1=makeQuery(id+"F24.opExtrude","CAP_EDGE",EDGE,{"disambiguationData":[OSD([subQ0]),TDD([makeQuery(id+"F22.imprint","IMPRINT",EDGE,{"disambiguationData":[TD([[makeQuery(id+"F22.imprint","INTERSECT",VERTEX,{"derivedFrom":[subQ0,sQuery(id+"F22.wireOp",EDGE,"E30")]}),1.0]])],"derivedFrom":subQ0})])],"isStart":false});}
            var Q2;
            {var subQ0=sQuery(id+"F22.wireOp",EDGE,"E24.top");Q2=makeQuery(id+"F24.opExtrude","CAP_EDGE",EDGE,{"disambiguationData":[OSD([subQ0]),TDD([makeQuery(id+"F22.imprint","IMPRINT",EDGE,{"disambiguationData":[TD([[makeQuery(id+"F22.imprint","INTERSECT",VERTEX,{"derivedFrom":[subQ0,sQuery(id+"F22.wireOp",EDGE,"E32")]}),1.0]])],"derivedFrom":subQ0})])],"isStart":false});}
            fillet(context, id + "F25", {"entities" : qUnion([Q0, Q1, Q2]), "tangentPropagation" : true, "radius" : 5 * mm, "defaultsChanged" : false, "vertexSettings" : [], "allowEdgeOverflow" : false});
        }
        {
            var Q0;
            Q0=qCreatedBy(makeId("Right.planeOp"),FACE);
            cPlane(context, id + "F26", {"entities" : qUnion([Q0]), "cplaneType" : CPlaneType.OFFSET, "offset" : 75 * mm, "oppositeDirection" : true, "width" : 150 * mm, "height" : 150 * mm});
        }
        {
            var Q0;
            Q0=qCreatedBy(id+"F26.planeOp",FACE);
            var sketch = newSketch(context, id + "F27", { "sketchPlane" : qUnion([Q0])});
            skLineSegment(sketch, "E44.bottom", {"start": v(75, 0) * mm, "end": v(-75, 0) * mm});
            skLineSegment(sketch, "E44.top", {"start": v(75, 200) * mm, "end": v(-75, 200) * mm});
            skLineSegment(sketch, "E44.left", {"start": v(75, 0) * mm, "end": v(75, 200) * mm});
            skLineSegment(sketch, "E44.right", {"start": v(-75, 0) * mm, "end": v(-75, 200) * mm});
            skCircle(sketch, "E45.0", {"center": v(0, 61) * mm, "radius": 6 * mm});
            skCircle(sketch, "E46.0", {"center": v(69.4, 166.74) * mm, "radius": 1.5 * mm});
            skCircle(sketch, "E47.0", {"center": v(69.4, 166.74) * mm, "radius": 1.75 * mm});
            skCircle(sketch, "E48.0", {"center": v(69.4, 8.54) * mm, "radius": 1.75 * mm});
            skCircle(sketch, "E49.0", {"center": v(69.4, 8.54) * mm, "radius": 1.5 * mm});
            skPoint(sketch, "E50.0", {"position": v(-69.4, 166.74) * mm});
            skCircle(sketch, "E51.0", {"center": v(-69.4, 166.74) * mm, "radius": 1.5 * mm});
            skCircle(sketch, "E52.0", {"center": v(-69.4, 166.74) * mm, "radius": 1.75 * mm});
            skCircle(sketch, "E53.0", {"center": v(-69.4, 8.54) * mm, "radius": 1.75 * mm});
            skCircle(sketch, "E54.0", {"center": v(-69.4, 8.54) * mm, "radius": 1.5 * mm});
            skSolve(sketch);
        }
        {
            var Q0;
            Q0=makeQuery(id+"F27.imprint","IMPRINT",FACE,{"disambiguationData":[TD([[makeQuery(id+"F27.imprint","IMPRINT",EDGE,{"derivedFrom":sQuery(id+"F27.wireOp",EDGE,"E44.bottom")}),-1.0]])]});
            var Q1;
            Q1=makeQuery(id+"F27.imprint","IMPRINT",FACE,{"disambiguationData":[TD([[makeQuery(id+"F27.imprint","IMPRINT",EDGE,{"derivedFrom":sQuery(id+"F27.wireOp",EDGE,"E53.0")}),1.0]])]});
            var Q2;
            Q2=makeQuery(id+"F27.imprint","IMPRINT",FACE,{"disambiguationData":[TD([[makeQuery(id+"F27.imprint","IMPRINT",EDGE,{"derivedFrom":sQuery(id+"F27.wireOp",EDGE,"E54.0")}),1.0]])]});
            var Q3;
            Q3=makeQuery(id+"F27.imprint","IMPRINT",FACE,{"disambiguationData":[TD([[makeQuery(id+"F27.imprint","IMPRINT",EDGE,{"derivedFrom":sQuery(id+"F27.wireOp",EDGE,"E49.0")}),-1.0]])]});
            var Q4;
            Q4=makeQuery(id+"F27.imprint","IMPRINT",FACE,{"disambiguationData":[TD([[makeQuery(id+"F27.imprint","IMPRINT",EDGE,{"derivedFrom":sQuery(id+"F27.wireOp",EDGE,"E48.0")}),-1.0]])]});
            var Q5;
            Q5=makeQuery(id+"F27.imprint","IMPRINT",FACE,{"disambiguationData":[TD([[makeQuery(id+"F27.imprint","IMPRINT",EDGE,{"derivedFrom":sQuery(id+"F27.wireOp",EDGE,"E46.0")}),-1.0]])]});
            var Q6;
            Q6=makeQuery(id+"F27.imprint","IMPRINT",FACE,{"disambiguationData":[TD([[makeQuery(id+"F27.imprint","IMPRINT",EDGE,{"derivedFrom":sQuery(id+"F27.wireOp",EDGE,"E46.0")}),1.0]])]});
            var Q7;
            Q7=makeQuery(id+"F27.imprint","IMPRINT",FACE,{"disambiguationData":[TD([[makeQuery(id+"F27.imprint","IMPRINT",EDGE,{"derivedFrom":sQuery(id+"F27.wireOp",EDGE,"E51.0")}),1.0]])]});
            var Q8;
            Q8=makeQuery(id+"F27.imprint","IMPRINT",FACE,{"disambiguationData":[TD([[makeQuery(id+"F27.imprint","IMPRINT",EDGE,{"derivedFrom":sQuery(id+"F27.wireOp",EDGE,"E51.0")}),-1.0]])]});
            extrude(context, id + "F28", {"entities" : qUnion([Q0, Q1, Q2, Q3, Q4, Q5, Q6, Q7, Q8]), "depth" : 1 * mm, "offsetDistance" : 25 * mm});
        }
        {
            var Q0;
            Q0=makeQuery(id+"F22.imprint","IMPRINT",FACE,{"disambiguationData":[TD([[makeQuery(id+"F22.imprint","IMPRINT",EDGE,{"derivedFrom":sQuery(id+"F22.wireOp",EDGE,"E36")}),-1.0]])]});
            var Q1;
            Q1=makeQuery(id+"F22.imprint","IMPRINT",FACE,{"disambiguationData":[TD([[makeQuery(id+"F22.imprint","IMPRINT",EDGE,{"derivedFrom":sQuery(id+"F22.wireOp",EDGE,"E36")}),1.0]])]});
            var Q2;
            Q2=makeQuery(id+"F22.imprint","IMPRINT",FACE,{"disambiguationData":[TD([[makeQuery(id+"F22.imprint","IMPRINT",EDGE,{"derivedFrom":sQuery(id+"F22.wireOp",EDGE,"E40.MirrorC")}),1.0]])]});
            var Q3;
            Q3=makeQuery(id+"F22.imprint","IMPRINT",FACE,{"disambiguationData":[TD([[makeQuery(id+"F22.imprint","IMPRINT",EDGE,{"derivedFrom":sQuery(id+"F22.wireOp",EDGE,"E40.MirrorC")}),-1.0]])]});
            var Q4;
            Q4=makeQuery(id+"F22.imprint","IMPRINT",FACE,{"disambiguationData":[TD([[makeQuery(id+"F22.imprint","IMPRINT",EDGE,{"derivedFrom":sQuery(id+"F22.wireOp",EDGE,"E42.MirrorC")}),-1.0]])]});
            var Q5;
            Q5=makeQuery(id+"F22.imprint","IMPRINT",FACE,{"disambiguationData":[TD([[makeQuery(id+"F22.imprint","IMPRINT",EDGE,{"derivedFrom":sQuery(id+"F22.wireOp",EDGE,"E42.MirrorC")}),1.0]])]});
            var Q6;
            Q6=makeQuery(id+"F22.imprint","IMPRINT",FACE,{"disambiguationData":[TD([[makeQuery(id+"F22.imprint","IMPRINT",EDGE,{"derivedFrom":sQuery(id+"F22.wireOp",EDGE,"E38")}),-1.0]])]});
            var Q7;
            Q7=makeQuery(id+"F22.imprint","IMPRINT",FACE,{"disambiguationData":[TD([[makeQuery(id+"F22.imprint","IMPRINT",EDGE,{"derivedFrom":sQuery(id+"F22.wireOp",EDGE,"E38")}),1.0]])]});
            extrude(context, id + "F29", {"entities" : qUnion([Q0, Q1, Q2, Q3, Q4, Q5, Q6, Q7]), "operationType" : NewBodyOperationType.REMOVE, "oppositeDirection" : true, "depth" : 5.5 * mm, "offsetDistance" : 25 * mm});
        }
        {
            var Q0;
            Q0=makeQuery(id+"F22.imprint","IMPRINT",FACE,{"disambiguationData":[TD([[makeQuery(id+"F22.imprint","IMPRINT",EDGE,{"derivedFrom":sQuery(id+"F22.wireOp",EDGE,"E38")}),1.0]])]});
            var Q1;
            Q1=makeQuery(id+"F22.imprint","IMPRINT",FACE,{"disambiguationData":[TD([[makeQuery(id+"F22.imprint","IMPRINT",EDGE,{"derivedFrom":sQuery(id+"F22.wireOp",EDGE,"E40.MirrorC")}),-1.0]])]});
            var Q2;
            Q2=makeQuery(id+"F22.imprint","IMPRINT",FACE,{"disambiguationData":[TD([[makeQuery(id+"F22.imprint","IMPRINT",EDGE,{"derivedFrom":sQuery(id+"F22.wireOp",EDGE,"E36")}),1.0]])]});
            var Q3;
            Q3=makeQuery(id+"F22.imprint","IMPRINT",FACE,{"disambiguationData":[TD([[makeQuery(id+"F22.imprint","IMPRINT",EDGE,{"derivedFrom":sQuery(id+"F22.wireOp",EDGE,"E42.MirrorC")}),-1.0]])]});
            extrude(context, id + "F30", {"entities" : qUnion([Q0, Q1, Q2, Q3]), "operationType" : NewBodyOperationType.ADD, "oppositeDirection" : true, "depth" : 5 * mm, "offsetDistance" : 25 * mm});
        }
        {
            var Q0;
            Q0=makeQuery(id+"F27.imprint","IMPRINT",FACE,{"disambiguationData":[TD([[makeQuery(id+"F27.imprint","IMPRINT",EDGE,{"derivedFrom":sQuery(id+"F27.wireOp",EDGE,"E46.0")}),1.0]])]});
            var Q1;
            Q1=makeQuery(id+"F27.imprint","IMPRINT",FACE,{"disambiguationData":[TD([[makeQuery(id+"F27.imprint","IMPRINT",EDGE,{"derivedFrom":sQuery(id+"F27.wireOp",EDGE,"E46.0")}),-1.0]])]});
            var Q2;
            Q2=makeQuery(id+"F27.imprint","IMPRINT",FACE,{"disambiguationData":[TD([[makeQuery(id+"F27.imprint","IMPRINT",EDGE,{"derivedFrom":sQuery(id+"F27.wireOp",EDGE,"E51.0")}),-1.0]])]});
            var Q3;
            Q3=makeQuery(id+"F27.imprint","IMPRINT",FACE,{"disambiguationData":[TD([[makeQuery(id+"F27.imprint","IMPRINT",EDGE,{"derivedFrom":sQuery(id+"F27.wireOp",EDGE,"E51.0")}),1.0]])]});
            var Q4;
            Q4=makeQuery(id+"F27.imprint","IMPRINT",FACE,{"disambiguationData":[TD([[makeQuery(id+"F27.imprint","IMPRINT",EDGE,{"derivedFrom":sQuery(id+"F27.wireOp",EDGE,"E48.0")}),-1.0]])]});
            var Q5;
            Q5=makeQuery(id+"F27.imprint","IMPRINT",FACE,{"disambiguationData":[TD([[makeQuery(id+"F27.imprint","IMPRINT",EDGE,{"derivedFrom":sQuery(id+"F27.wireOp",EDGE,"E49.0")}),-1.0]])]});
            var Q6;
            Q6=makeQuery(id+"F27.imprint","IMPRINT",FACE,{"disambiguationData":[TD([[makeQuery(id+"F27.imprint","IMPRINT",EDGE,{"derivedFrom":sQuery(id+"F27.wireOp",EDGE,"E53.0")}),1.0]])]});
            var Q7;
            Q7=makeQuery(id+"F27.imprint","IMPRINT",FACE,{"disambiguationData":[TD([[makeQuery(id+"F27.imprint","IMPRINT",EDGE,{"derivedFrom":sQuery(id+"F27.wireOp",EDGE,"E54.0")}),1.0]])]});
            extrude(context, id + "F31", {"entities" : qUnion([Q0, Q1, Q2, Q3, Q4, Q5, Q6, Q7]), "operationType" : NewBodyOperationType.REMOVE, "depth" : 5.5 * mm, "offsetDistance" : 25 * mm});
        }
        {
            var Q0;
            Q0=makeQuery(id+"F27.imprint","IMPRINT",FACE,{"disambiguationData":[TD([[makeQuery(id+"F27.imprint","IMPRINT",EDGE,{"derivedFrom":sQuery(id+"F27.wireOp",EDGE,"E49.0")}),-1.0]])]});
            var Q1;
            Q1=makeQuery(id+"F27.imprint","IMPRINT",FACE,{"disambiguationData":[TD([[makeQuery(id+"F27.imprint","IMPRINT",EDGE,{"derivedFrom":sQuery(id+"F27.wireOp",EDGE,"E54.0")}),1.0]])]});
            var Q2;
            Q2=makeQuery(id+"F27.imprint","IMPRINT",FACE,{"disambiguationData":[TD([[makeQuery(id+"F27.imprint","IMPRINT",EDGE,{"derivedFrom":sQuery(id+"F27.wireOp",EDGE,"E46.0")}),-1.0]])]});
            var Q3;
            Q3=makeQuery(id+"F27.imprint","IMPRINT",FACE,{"disambiguationData":[TD([[makeQuery(id+"F27.imprint","IMPRINT",EDGE,{"derivedFrom":sQuery(id+"F27.wireOp",EDGE,"E51.0")}),1.0]])]});
            extrude(context, id + "F32", {"entities" : qUnion([Q0, Q1, Q2, Q3]), "operationType" : NewBodyOperationType.ADD, "depth" : 5 * mm, "offsetDistance" : 25 * mm});
        }
        {
            var Q0;
            Q0=makeQuery(id+"F19.opExtrude","SWEPT_BODY",BODY,{"disambiguationData":[OSD([sQuery(id+"F18.wireOp",EDGE,"E17.bottom"),sQuery(id+"F18.wireOp",EDGE,"E17.top"),sQuery(id+"F18.wireOp",EDGE,"E17.right"),sQuery(id+"F18.wireOp",EDGE,"E19")])]});
            var Q1;
            Q1=qCreatedBy(makeId("Front.planeOp"),FACE);
            mirror(context, id + "F33", {"entities" : qUnion([Q0]), "mirrorPlane" : qUnion([Q1])});
        }
        {
            var Q0;
            Q0=qCreatedBy(makeId("Top.planeOp"),FACE);
            cPlane(context, id + "F34", {"entities" : qUnion([Q0]), "cplaneType" : CPlaneType.OFFSET, "offset" : 100 * mm, "width" : 150 * mm, "height" : 150 * mm});
        }
        {
            var Q0;
            Q0=qCreatedBy(id+"F34.planeOp",FACE);
            var sketch = newSketch(context, id + "F35", { "sketchPlane" : qUnion([Q0])});
            skLineSegment(sketch, "E55.0", {"start": v(74, -75) * mm, "end": v(74, -20) * mm});
            skLineSegment(sketch, "E56.0", {"start": v(64, -65) * mm, "end": v(74, -65) * mm});
            skLineSegment(sketch, "E57.0", {"start": v(64, 65) * mm, "end": v(74, 65) * mm});
            skLineSegment(sketch, "E58.0", {"start": v(-74, 57) * mm, "end": v(-74, -57) * mm});
            skLineSegment(sketch, "E59.0", {"start": v(-64, 65) * mm, "end": v(-74, 65) * mm});
            skLineSegment(sketch, "E60.0", {"start": v(-64, -65) * mm, "end": v(-74, -65) * mm});
            skLineSegment(sketch, "E61.bottom", {"start": v(-74, -65) * mm, "end": v(-61.5, -65) * mm});
            skLineSegment(sketch, "E61.top", {"start": v(-69, -62) * mm, "end": v(-61.5, -62) * mm});
            skLineSegment(sketch, "E61.left", {"start": v(-74, -65) * mm, "end": v(-74, -62) * mm});
            skLineSegment(sketch, "E61.right", {"start": v(-61.5, -65) * mm, "end": v(-61.5, -62) * mm});
            skLineSegment(sketch, "E62", {"start": v(-63.7, -65) * mm, "end": v(-63.7, -65.5) * mm});
            skLineSegment(sketch, "E63", {"start": v(-63.7, -65.5) * mm, "end": v(-61.5, -65) * mm});
            skPoint(sketch, "E64.newPointA", {"position": v(-74, -75) * mm});
            skArc(sketch, "E64.filletArc", {"start": v(-74, -57) * mm, "mid": v(-72.54, -60.54) * mm, "end": v(-69, -62) * mm});
            skLineSegment(sketch, "E65.bottom", {"start": v(-74, 65) * mm, "end": v(-61.5, 65) * mm});
            skLineSegment(sketch, "E65.top", {"start": v(-69, 62) * mm, "end": v(-61.5, 62) * mm});
            skLineSegment(sketch, "E65.left", {"start": v(-74, 65) * mm, "end": v(-74, 62) * mm});
            skLineSegment(sketch, "E65.right", {"start": v(-61.5, 65) * mm, "end": v(-61.5, 62) * mm});
            skLineSegment(sketch, "E66", {"start": v(-63.7, 65) * mm, "end": v(-63.7, 65.5) * mm});
            skLineSegment(sketch, "E67", {"start": v(-63.7, 65.5) * mm, "end": v(-61.5, 65) * mm});
            skPoint(sketch, "E68.newPointB", {"position": v(-74, 75) * mm});
            skArc(sketch, "E68.filletArc", {"start": v(-69, 62) * mm, "mid": v(-72.54, 60.54) * mm, "end": v(-74, 57) * mm});
            skLineSegment(sketch, "E69.MirrorCS", {"start": v(63.7, -65) * mm, "end": v(63.7, -65.5) * mm});
            skLineSegment(sketch, "E70.MirrorCS", {"start": v(74, -65) * mm, "end": v(74, -62) * mm});
            skLineSegment(sketch, "E71.MirrorCS", {"start": v(61.5, -65) * mm, "end": v(61.5, -62) * mm});
            skLineSegment(sketch, "E72.MirrorCS", {"start": v(69, -62) * mm, "end": v(61.5, -62) * mm});
            skArc(sketch, "E73.MirrorCS", {"start": v(74, -57) * mm, "mid": v(72.54, -60.54) * mm, "end": v(69, -62) * mm});
            skLineSegment(sketch, "E74.MirrorCS", {"start": v(63.7, -65.5) * mm, "end": v(61.5, -65) * mm});
            skLineSegment(sketch, "E75.MirrorCS", {"start": v(74, -65) * mm, "end": v(61.5, -65) * mm});
            skLineSegment(sketch, "E76.MirrorCS", {"start": v(61.5, 65) * mm, "end": v(61.5, 62) * mm});
            skLineSegment(sketch, "E77.MirrorCS", {"start": v(63.7, 65.5) * mm, "end": v(61.5, 65) * mm});
            skLineSegment(sketch, "E78.MirrorCS", {"start": v(63.7, 65) * mm, "end": v(63.7, 65.5) * mm});
            skLineSegment(sketch, "E79.MirrorCS", {"start": v(74, 65) * mm, "end": v(74, 62) * mm});
            skLineSegment(sketch, "E80.MirrorCS", {"start": v(69, 62) * mm, "end": v(61.5, 62) * mm});
            skArc(sketch, "E81.MirrorCS", {"start": v(69, 62) * mm, "mid": v(72.54, 60.54) * mm, "end": v(74, 57) * mm});
            skLineSegment(sketch, "E82.MirrorCS", {"start": v(74, 65) * mm, "end": v(61.5, 65) * mm});
            skLineSegment(sketch, "E83.bottom", {"start": v(-74, -57) * mm, "end": v(-75, -57) * mm});
            skLineSegment(sketch, "E83.top", {"start": v(-74, -65) * mm, "end": v(-75, -65) * mm});
            skLineSegment(sketch, "E83.left", {"start": v(-74, -57) * mm, "end": v(-74, -65) * mm});
            skLineSegment(sketch, "E83.right", {"start": v(-75, -57) * mm, "end": v(-75, -65) * mm});
            skLineSegment(sketch, "E84", {"start": v(-74, 65) * mm, "end": v(-74, 57) * mm});
            skLineSegment(sketch, "E85", {"start": v(74, 65) * mm, "end": v(74, 57) * mm});
            skLineSegment(sketch, "E86", {"start": v(74, -57) * mm, "end": v(74, -65) * mm});
            skSolve(sketch);
        }
        {
            var Q0;
            {var subQ1=sQuery(id+"F35.wireOp",EDGE,"E60.0");Q0=makeQuery(id+"F35.imprint","IMPRINT",FACE,{"disambiguationData":[TD([[makeQuery(id+"F35.imprint","IMPRINT",EDGE,{"derivedFrom":subQ1}),-1.0]])]});}
            var Q1;
            {var subQ0=sQuery(id+"F35.wireOp",EDGE,"E62");Q1=makeQuery(id+"F35.imprint","IMPRINT",FACE,{"disambiguationData":[TD([[makeQuery(id+"F35.imprint","IMPRINT",EDGE,{"derivedFrom":subQ0}),1.0]])]});}
            var Q2;
            {var subQ0=sQuery(id+"F35.wireOp",EDGE,"E66");Q2=makeQuery(id+"F35.imprint","IMPRINT",FACE,{"disambiguationData":[TD([[makeQuery(id+"F35.imprint","IMPRINT",EDGE,{"derivedFrom":subQ0}),-1.0]])]});}
            var Q3;
            {var subQ1=sQuery(id+"F35.wireOp",EDGE,"E59.0");Q3=makeQuery(id+"F35.imprint","IMPRINT",FACE,{"disambiguationData":[TD([[makeQuery(id+"F35.imprint","IMPRINT",EDGE,{"derivedFrom":subQ1}),1.0]])]});}
            extrude(context, id + "F36", {"entities" : qUnion([Q0, Q1, Q2, Q3]), "operationType" : NewBodyOperationType.ADD, "depth" : 20 * mm, "offsetDistance" : 25 * mm});
        }
        {
            var Q0;
            {var subQ1=sQuery(id+"F35.wireOp",EDGE,"E57.0");Q0=makeQuery(id+"F35.imprint","IMPRINT",FACE,{"disambiguationData":[TD([[makeQuery(id+"F35.imprint","IMPRINT",EDGE,{"derivedFrom":subQ1}),-1.0]])]});}
            var Q1;
            {var subQ0=sQuery(id+"F35.wireOp",EDGE,"E77.MirrorCS");Q1=makeQuery(id+"F35.imprint","IMPRINT",FACE,{"disambiguationData":[TD([[makeQuery(id+"F35.imprint","IMPRINT",EDGE,{"derivedFrom":subQ0}),1.0]])]});}
            var Q2;
            {var subQ3=sQuery(id+"F35.wireOp",EDGE,"E56.0");Q2=makeQuery(id+"F35.imprint","IMPRINT",FACE,{"disambiguationData":[TD([[makeQuery(id+"F35.imprint","IMPRINT",EDGE,{"derivedFrom":subQ3}),1.0]])]});}
            var Q3;
            {var subQ0=sQuery(id+"F35.wireOp",EDGE,"E69.MirrorCS");Q3=makeQuery(id+"F35.imprint","IMPRINT",FACE,{"disambiguationData":[TD([[makeQuery(id+"F35.imprint","IMPRINT",EDGE,{"derivedFrom":subQ0}),-1.0]])]});}
            extrude(context, id + "F37", {"entities" : qUnion([Q0, Q1, Q2, Q3]), "operationType" : NewBodyOperationType.ADD, "depth" : 20 * mm, "offsetDistance" : 25 * mm});
        }
    });
